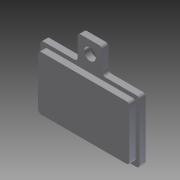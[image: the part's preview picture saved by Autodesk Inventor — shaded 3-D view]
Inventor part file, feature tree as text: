
AUTODESK INVENTOR PART (.ipt)
format: ipt  version: 2011 (Build 150239000, 239)  size: 120,320 bytes
history: native  units: in
note: dims shown in document units (in); Inventor stores cm internally (conversion verified against a paired STEP export)
features: sketch x4, extrude x3, hole x1, fillet x1
ambient origin geometry x8: Origin, YZ Plane, XZ Plane, XY Plane, X Axis, Y Axis, Z Axis, Center Point
bodies: Solid1 (feature_tree)
feature tree (9):
  extrude  "Extrusion1"  Depth=0.3937in
  extrude  "Extrusion2"  Depth=0.025in
  extrude  "Extrusion3"  Depth=0.1575in
  hole  "Hole1"  [1 undecoded]
  fillet  "Fillet1"  Radius=0.0197in
  sketch  "Sketch1"  dims[d0=0.6299in d1=0.3937in]
  sketch  "Sketch2"  dims[d2=0.0787in d3=0.0in d4=0.025in]
  sketch  "Sketch3"  dims[d5=0.0394in d6=0.0in d7=0.1575in]
  sketch  "Sketch4"  dims[d8=0.2362in d9=0.1575in d10=0.0in d11=0.075in d12=0.75in d13=0.375in d14=0.25in d15=0.5635in d16=1.0in d17=0.8108in d18=0.0197in]
note: 1 required parameter value undecoded (feature->parameter linkage not recoverable at this tier; creation-order binding heuristic only, values carry confidence <= 0.55)
